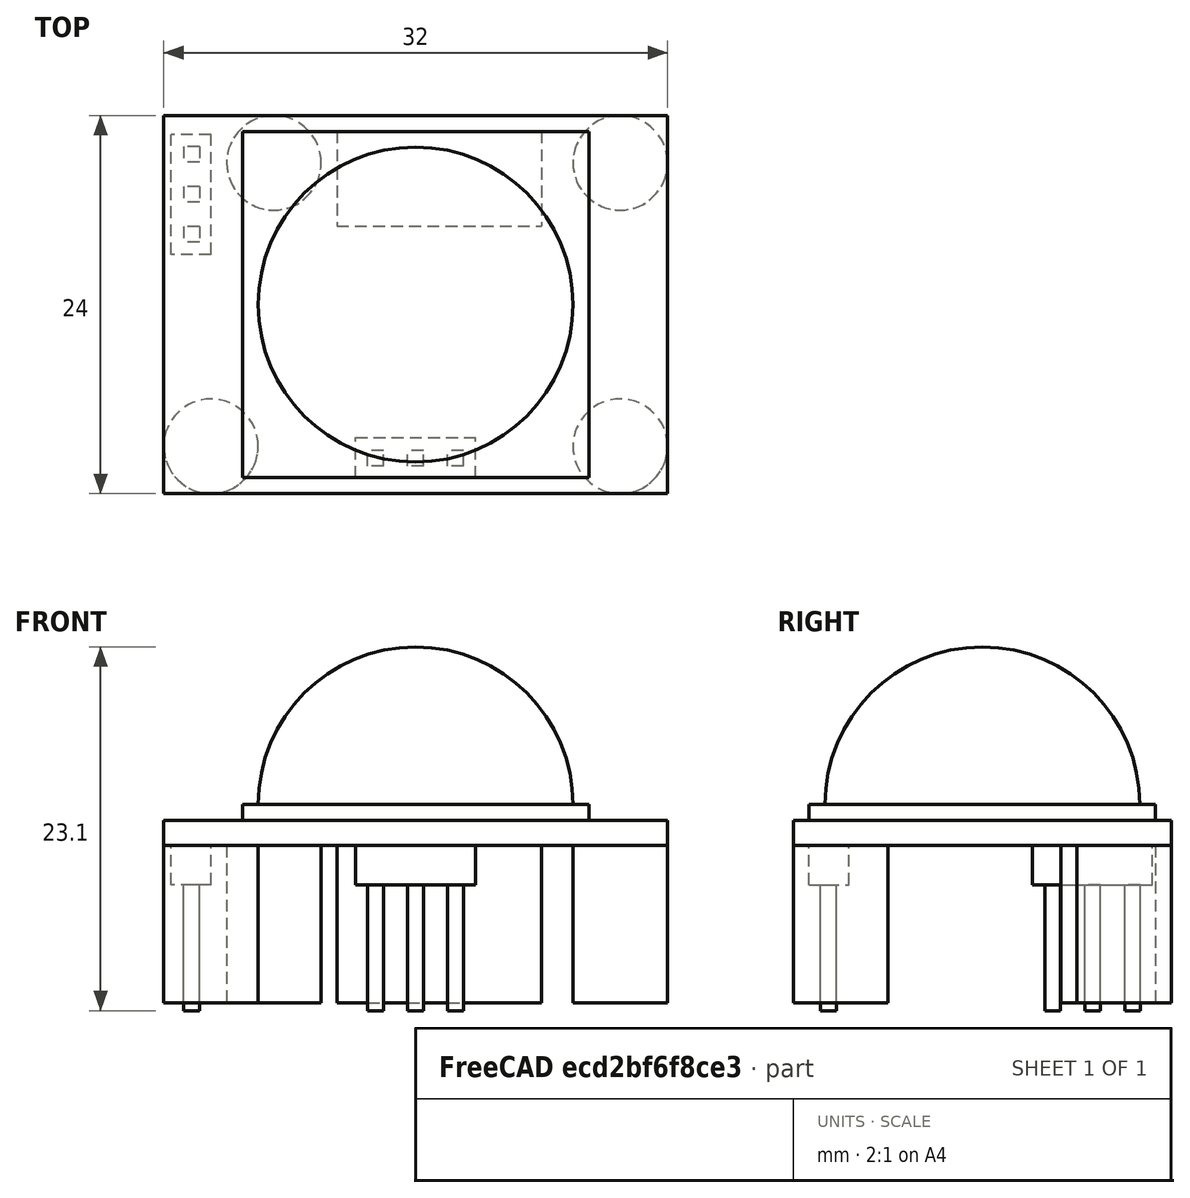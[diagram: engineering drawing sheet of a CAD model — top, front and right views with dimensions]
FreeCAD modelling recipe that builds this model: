
FCSTD DOCUMENT  (FreeCAD 0.14R3702 (Git))
Label: hc-sr501
License: CC-BY 3.0
LicenseURL: http://creativecommons.org/licenses/by/3.0/
objects: Part::FeaturePython×6, Part::Box×5, Part::MultiFuse×3, Part::Sphere×1, Part::Cylinder×1
note: 16 computed .brp shape members not serialized (recipe doc carries the construction recipe); baked Part::Feature solids carry a one-line shape summary decoded from their .brp

FEATURE [Part::Box] Box  label="Cube"
  Height = 1.6
  Length = 32
  Placement = pos=(-16,-12,0) rot=(0,0,1;0rad)
  Width = 24
FEATURE [Part::Box] Box001  label="Cube001"
  Height = 1
  Length = 22
  Placement = pos=(-11,-11,1.6) rot=(0,0,1;0rad)
  Width = 22
FEATURE [Part::Sphere] Sphere
  Angle1 = 0
  Angle2 = 90
  Angle3 = 360
  Placement = pos=(0,0,2.6) rot=(0,0,1;0rad)
  Radius = 10
FEATURE [Part::Box] Box002  label="Cube002"
  Height = 2.5
  Length = 7.62
  Placement = pos=(-3.81,-11,-2.5) rot=(0,0,1;0rad)
  Width = 2.54
FEATURE [Part::Cylinder] Cylinder
  Angle = 360
  Height = 10
  Placement = pos=(13,9,0) rot=(1,0,0;3.14159rad)
  Radius = 3
FEATURE [Part::FeaturePython] Clone  label="Clone of Cylinder"  # Draft clone (typed FeaturePython)
  Objects = -> [Cylinder]
  Placement = pos=(13,-9,0) rot=(1,0,0;3.14159rad)
  Scale = (1,1,1)
FEATURE [Part::FeaturePython] Clone001  label="Clone of Cylinder001"  # Draft clone (typed FeaturePython)
  Objects = -> [Cylinder]
  Placement = pos=(-13,-9,0) rot=(1,0,0;3.14159rad)
  Scale = (1,1,1)
FEATURE [Part::FeaturePython] Clone002  label="Clone of Cylinder002"  # Draft clone (typed FeaturePython)
  Objects = -> [Cylinder]
  Placement = pos=(-9,9,0) rot=(1,0,0;3.14159rad)
  Scale = (1,1,1)
FEATURE [Part::Box] Box003  label="Cube003"
  Height = 8.5
  Length = 1
  Placement = pos=(2.04,-10.27,-10.5) rot=(0,0,1;0rad)
  Width = 1
FEATURE [Part::FeaturePython] Clone003  label="Clone of Cube003"  # Draft clone (typed FeaturePython)
  Objects = -> [Box003]
  Placement = pos=(-3.04,-10.27,-10.5) rot=(0,0,1;0rad)
  Scale = (1,1,1)
FEATURE [Part::FeaturePython] Clone004  label="Clone of Cube004"  # Draft clone (typed FeaturePython)
  Objects = -> [Box003]
  Placement = pos=(-0.5,-10.27,-10.5) rot=(0,0,1;0rad)
  Scale = (1,1,1)
FEATURE [Part::MultiFuse] Fusion
  Shapes = -> [Box002,Clone003,Clone004,Box003]
FEATURE [Part::FeaturePython] Clone005  label="Clone of Fusion"  # Draft clone (typed FeaturePython)
  Objects = -> [Fusion]
  Placement = pos=(-24,7,0) rot=(0,0,1;1.5708rad)
  Scale = (1,1,1)
FEATURE [Part::Box] Box004  label="Cube004"
  Height = 10
  Length = 13
  Placement = pos=(-5,11,0) rot=(1,0,0;3.14159rad)
  Width = 6
FEATURE [Part::MultiFuse] Fusion001
  Shapes = -> [Box001,Sphere]
FEATURE [Part::MultiFuse] Fusion002  label="hc-sr501"
  Shapes = -> [Clone005,Clone002,Box004,Cylinder,Clone,Fusion,Clone001,Box,Fusion001]
